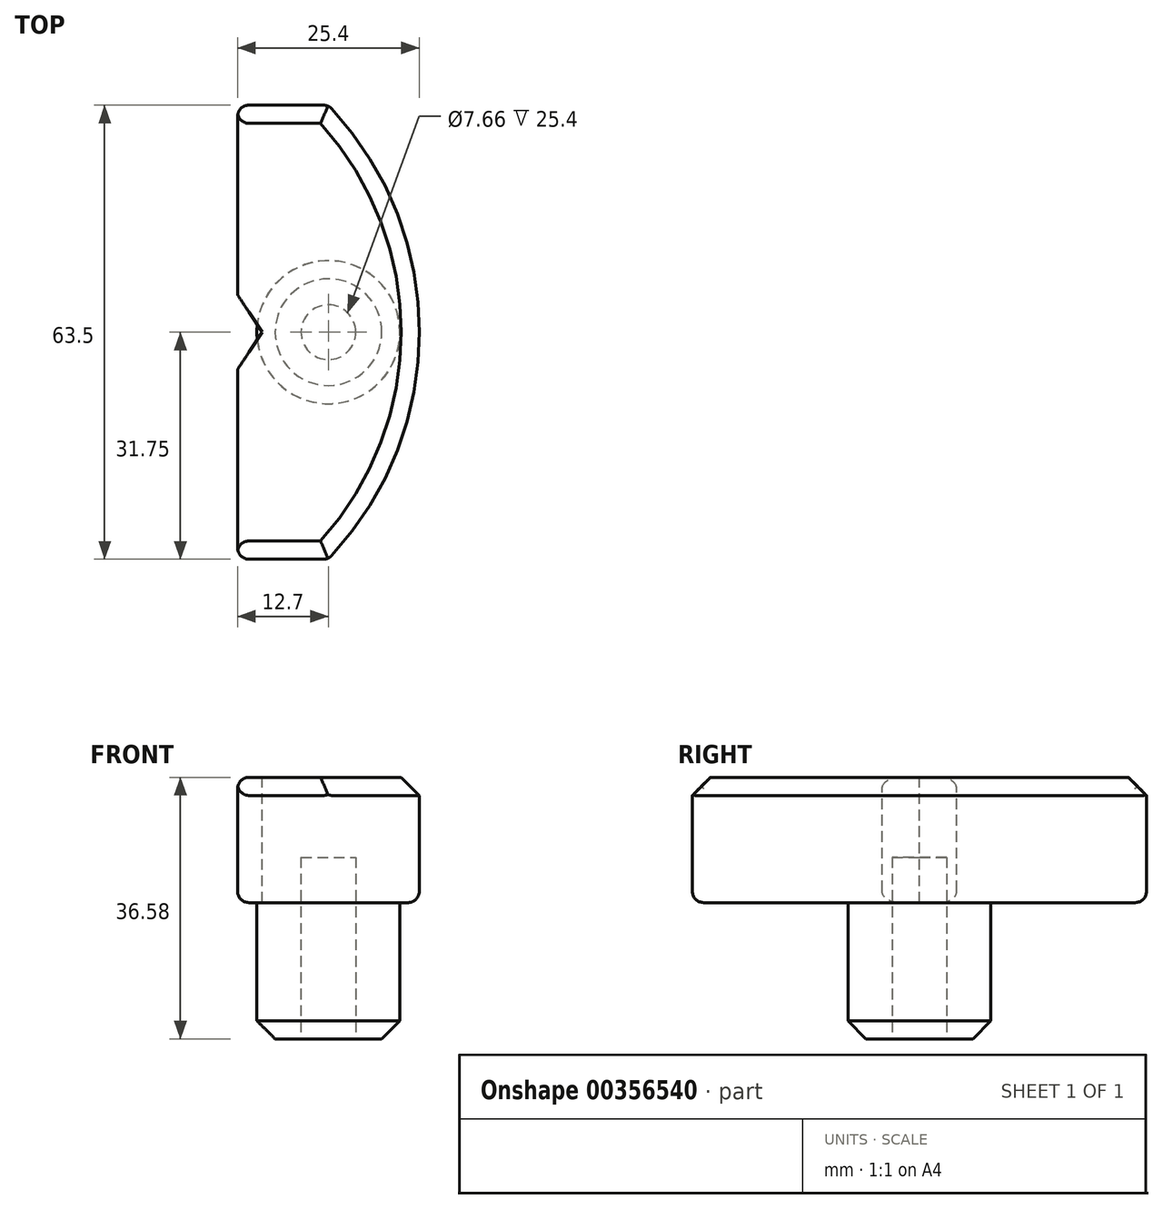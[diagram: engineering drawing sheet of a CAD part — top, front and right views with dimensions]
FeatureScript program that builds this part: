
annotation { "Feature Type Name" : "Feature", "Feature Type Description" : "" }
export const myFeature = defineFeature(function(context is Context, id is Id, definition is map)
    precondition{}
    {
        {
            var Q0;
            Q0=qCreatedBy(makeId("Top.planeOp"),FACE);
            var sketch = newSketch(context, id + "F0", { "sketchPlane" : qUnion([Q0])});
            skLineSegment(sketch, "E0", {"start": v(0, -31.75) * mm, "end": v(0, 31.75) * mm});
            skLineSegment(sketch, "E1", {"start": v(0, 31.75) * mm, "end": v(12.7, 31.75) * mm});
            skLineSegment(sketch, "E2", {"start": v(0, -31.75) * mm, "end": v(12.7, -31.75) * mm});
            skArc(sketch, "E3", {"start": v(12.7, -31.75) * mm, "mid": v(25.4, 0) * mm, "end": v(12.7, 31.75) * mm});
            skSolve(sketch);
        }
        {
            var Q0;
            Q0 = qSketchRegion(id + "F0", true);
            extrude(context, id + "F1", {"entities" : qUnion([Q0]), "depth" : 17.53 * mm});
        }
        {
            var Q0;
            Q0=makeQuery(id+"F1.opExtrude","CAP_FACE",FACE,{"disambiguationData":[OSD([sQuery(id+"F0.wireOp",EDGE,"E0"),sQuery(id+"F0.wireOp",EDGE,"E1"),sQuery(id+"F0.wireOp",EDGE,"E2"),sQuery(id+"F0.wireOp",EDGE,"E3")])],"isStart":true});
            var sketch = newSketch(context, id + "F2", { "sketchPlane" : qUnion([Q0])});
            skCircle(sketch, "E4", {"center": v(12.7, 0) * mm, "radius": 10 * mm});
            skSolve(sketch);
        }
        {
            var Q0;
            {var subQ0=sQuery(id+"F2.wireOp",EDGE,"E4");var subQ1=makeQuery(id+"F1.opExtrude","CAP_EDGE",EDGE,{"disambiguationData":[OSD([sQuery(id+"F0.wireOp",EDGE,"E3")])],"isStart":true});var subQ2=makeQuery(id+"F2.imprint","INTERSECT",VERTEX,{"disambiguationData":[OD(0.0)],"derivedFrom":[subQ1,subQ0]});Q0=makeQuery(id+"F2.imprint","IMPRINT",FACE,{"disambiguationData":[TD([[makeQuery(id+"F2.imprint","IMPRINT",EDGE,{"disambiguationData":[TD([[subQ2,1.0]])],"derivedFrom":subQ0}),1.0]])]});}
            var Q1;
            {var subQ0=sQuery(id+"F2.wireOp",EDGE,"E4");var subQ1=makeQuery(id+"F1.opExtrude","CAP_EDGE",EDGE,{"disambiguationData":[OSD([sQuery(id+"F0.wireOp",EDGE,"E3")])],"isStart":true});var subQ2=makeQuery(id+"F2.imprint","INTERSECT",VERTEX,{"disambiguationData":[OD(0.0)],"derivedFrom":[subQ1,subQ0]});Q1=makeQuery(id+"F2.imprint","IMPRINT",FACE,{"disambiguationData":[TD([[makeQuery(id+"F2.imprint","IMPRINT",EDGE,{"disambiguationData":[TD([[subQ2,-1.0]])],"derivedFrom":subQ0}),1.0]])]});}
            extrude(context, id + "F3", {"entities" : qUnion([Q0, Q1]), "operationType" : NewBodyOperationType.ADD, "depth" : 19.05 * mm});
        }
        {
            var Q0;
            Q0=makeQuery(id+"F1.opExtrude","CAP_EDGE",EDGE,{"disambiguationData":[OSD([sQuery(id+"F0.wireOp",EDGE,"E3")])],"isStart":false});
            var Q1;
            Q1=makeQuery(id+"F1.opExtrude","CAP_EDGE",EDGE,{"disambiguationData":[OSD([sQuery(id+"F0.wireOp",EDGE,"E2")])],"isStart":false});
            var Q2;
            Q2=makeQuery(id+"F1.opExtrude","CAP_EDGE",EDGE,{"disambiguationData":[OSD([sQuery(id+"F0.wireOp",EDGE,"E1")])],"isStart":false});
            chamfer(context, id + "F4", {"entities" : qUnion([Q0, Q1, Q2]), "width" : 2.54 * mm, "tangentPropagation" : true});
        }
        {
            var Q0;
            Q0=makeQuery(id+"F3.opExtrude","CAP_EDGE",EDGE,{"disambiguationData":[OSD([sQuery(id+"F2.wireOp",EDGE,"E4")])],"isStart":false});
            chamfer(context, id + "F5", {"entities" : qUnion([Q0]), "width" : 2.54 * mm, "tangentPropagation" : true});
        }
        {
            var Q0;
            Q0=makeQuery(id+"F3.opExtrude","CAP_FACE",FACE,{"disambiguationData":[OSD([sQuery(id+"F2.wireOp",EDGE,"E4")])],"isStart":false});
            var sketch = newSketch(context, id + "F6", { "sketchPlane" : qUnion([Q0])});
            skCircle(sketch, "E5", {"center": v(12.7, 0) * mm, "radius": 3.83 * mm});
            skSolve(sketch);
        }
        {
            var Q0;
            Q0 = qSketchRegion(id + "F6", true);
            extrude(context, id + "F7", {"entities" : qUnion([Q0]), "operationType" : NewBodyOperationType.REMOVE, "oppositeDirection" : true, "depth" : 25.4 * mm});
        }
        {
            var Q0;
            Q0=makeQuery(id+"F1.opExtrude","CAP_FACE",FACE,{"disambiguationData":[OSD([sQuery(id+"F0.wireOp",EDGE,"E0"),sQuery(id+"F0.wireOp",EDGE,"E1"),sQuery(id+"F0.wireOp",EDGE,"E2"),sQuery(id+"F0.wireOp",EDGE,"E3")])],"isStart":false});
            var sketch = newSketch(context, id + "F8", { "sketchPlane" : qUnion([Q0])});
            skLineSegment(sketch, "E6", {"start": v(3.43, 0) * mm, "end": v(0, 5.22) * mm});
            skLineSegment(sketch, "E7", {"start": v(0, 5.22) * mm, "end": v(0, 0) * mm});
            skLineSegment(sketch, "E8.MirrorCS", {"start": v(3.43, 0) * mm, "end": v(0, -5.22) * mm});
            skLineSegment(sketch, "E9.MirrorCS", {"start": v(0, -5.22) * mm, "end": v(0, 0) * mm});
            skSolve(sketch);
        }
        {
            var Q0;
            Q0 = qSketchRegion(id + "F8", true);
            var Q1;
            Q1=makeQuery(id+"F1.opExtrude","CAP_FACE",FACE,{"disambiguationData":[OSD([sQuery(id+"F0.wireOp",EDGE,"E0"),sQuery(id+"F0.wireOp",EDGE,"E1"),sQuery(id+"F0.wireOp",EDGE,"E2"),sQuery(id+"F0.wireOp",EDGE,"E3")])],"isStart":true});
            extrude(context, id + "F9", {"entities" : qUnion([Q0]), "operationType" : NewBodyOperationType.REMOVE, "endBound" : BoundingType.UP_TO_SURFACE, "oppositeDirection" : true, "endBoundEntityFace" : qUnion([Q1]), "depth" : 25.4 * mm});
        }
        {
            var Q0;
            {var subQ0=sQuery(id+"F0.wireOp",EDGE,"E0");var subQ1=sQuery(id+"F0.wireOp",EDGE,"E1");Q0=makeQuery(id+"F9.boolean.opBoolean","SPLIT",EDGE,{"disambiguationData":[TD([makeQuery(id+"F1.opExtrude","SWEPT_FACE",FACE,{"disambiguationData":[OSD([subQ1])]})])],"derivedFrom":makeQuery(id+"F1.opExtrude","CAP_EDGE",EDGE,{"disambiguationData":[OSD([subQ0])],"isStart":true})});}
            var Q1;
            Q1=makeQuery(id+"F1.opExtrude","CAP_EDGE",EDGE,{"disambiguationData":[OSD([sQuery(id+"F0.wireOp",EDGE,"E1")])],"isStart":true});
            var Q2;
            Q2=makeQuery(id+"F1.opExtrude","CAP_EDGE",EDGE,{"disambiguationData":[OSD([sQuery(id+"F0.wireOp",EDGE,"E3")])],"isStart":true});
            var Q3;
            {var subQ0=sQuery(id+"F0.wireOp",EDGE,"E0");var subQ1=sQuery(id+"F0.wireOp",EDGE,"E2");Q3=makeQuery(id+"F9.boolean.opBoolean","SPLIT",EDGE,{"disambiguationData":[TD([makeQuery(id+"F1.opExtrude","SWEPT_FACE",FACE,{"disambiguationData":[OSD([subQ1])]})])],"derivedFrom":makeQuery(id+"F1.opExtrude","CAP_EDGE",EDGE,{"disambiguationData":[OSD([subQ0])],"isStart":true})});}
            var Q4;
            Q4=makeQuery(id+"F1.opExtrude","CAP_EDGE",EDGE,{"disambiguationData":[OSD([sQuery(id+"F0.wireOp",EDGE,"E2")])],"isStart":true});
            var Q5;
            Q5=makeQuery(id+"F1.opExtrude","SWEPT_EDGE",EDGE,{"disambiguationData":[OSD([sQuery(id+"F0.wireOp",EDGE,"E0"),sQuery(id+"F0.wireOp",EDGE,"E2")])]});
            var Q6;
            Q6=makeQuery(id+"F1.opExtrude","SWEPT_EDGE",EDGE,{"disambiguationData":[OSD([sQuery(id+"F0.wireOp",EDGE,"E0"),sQuery(id+"F0.wireOp",EDGE,"E1")])]});
            var Q7;
            Q7=makeQuery(id+"F1.opExtrude","SWEPT_EDGE",EDGE,{"disambiguationData":[OSD([sQuery(id+"F0.wireOp",EDGE,"E1"),sQuery(id+"F0.wireOp",EDGE,"E3")])]});
            var Q8;
            Q8=makeQuery(id+"F1.opExtrude","SWEPT_EDGE",EDGE,{"disambiguationData":[OSD([sQuery(id+"F0.wireOp",EDGE,"E2"),sQuery(id+"F0.wireOp",EDGE,"E3")])]});
            var Q9;
            {var subQ0=sQuery(id+"F0.wireOp",EDGE,"E0");var subQ1=sQuery(id+"F0.wireOp",EDGE,"E2");Q9=makeQuery(id+"F9.boolean.opBoolean","SPLIT",EDGE,{"disambiguationData":[TD([makeQuery(id+"F4.opChamfer","BLEND_FACE",FACE,{"disambiguationData":[OSD([subQ1])]})])],"derivedFrom":makeQuery(id+"F1.opExtrude","CAP_EDGE",EDGE,{"disambiguationData":[OSD([subQ0])],"isStart":false})});}
            var Q10;
            {var subQ0=sQuery(id+"F0.wireOp",EDGE,"E0");var subQ1=sQuery(id+"F0.wireOp",EDGE,"E1");Q10=makeQuery(id+"F9.boolean.opBoolean","SPLIT",EDGE,{"disambiguationData":[TD([makeQuery(id+"F4.opChamfer","BLEND_FACE",FACE,{"disambiguationData":[OSD([subQ1])]})])],"derivedFrom":makeQuery(id+"F1.opExtrude","CAP_EDGE",EDGE,{"disambiguationData":[OSD([subQ0])],"isStart":false})});}
            fillet(context, id + "F10", {"entities" : qUnion([Q0, Q1, Q2, Q3, Q4, Q5, Q6, Q7, Q8, Q9, Q10]), "radius" : 1.59 * mm, "tangentPropagation" : true, "allowEdgeOverflow" : false});
        }
    });
